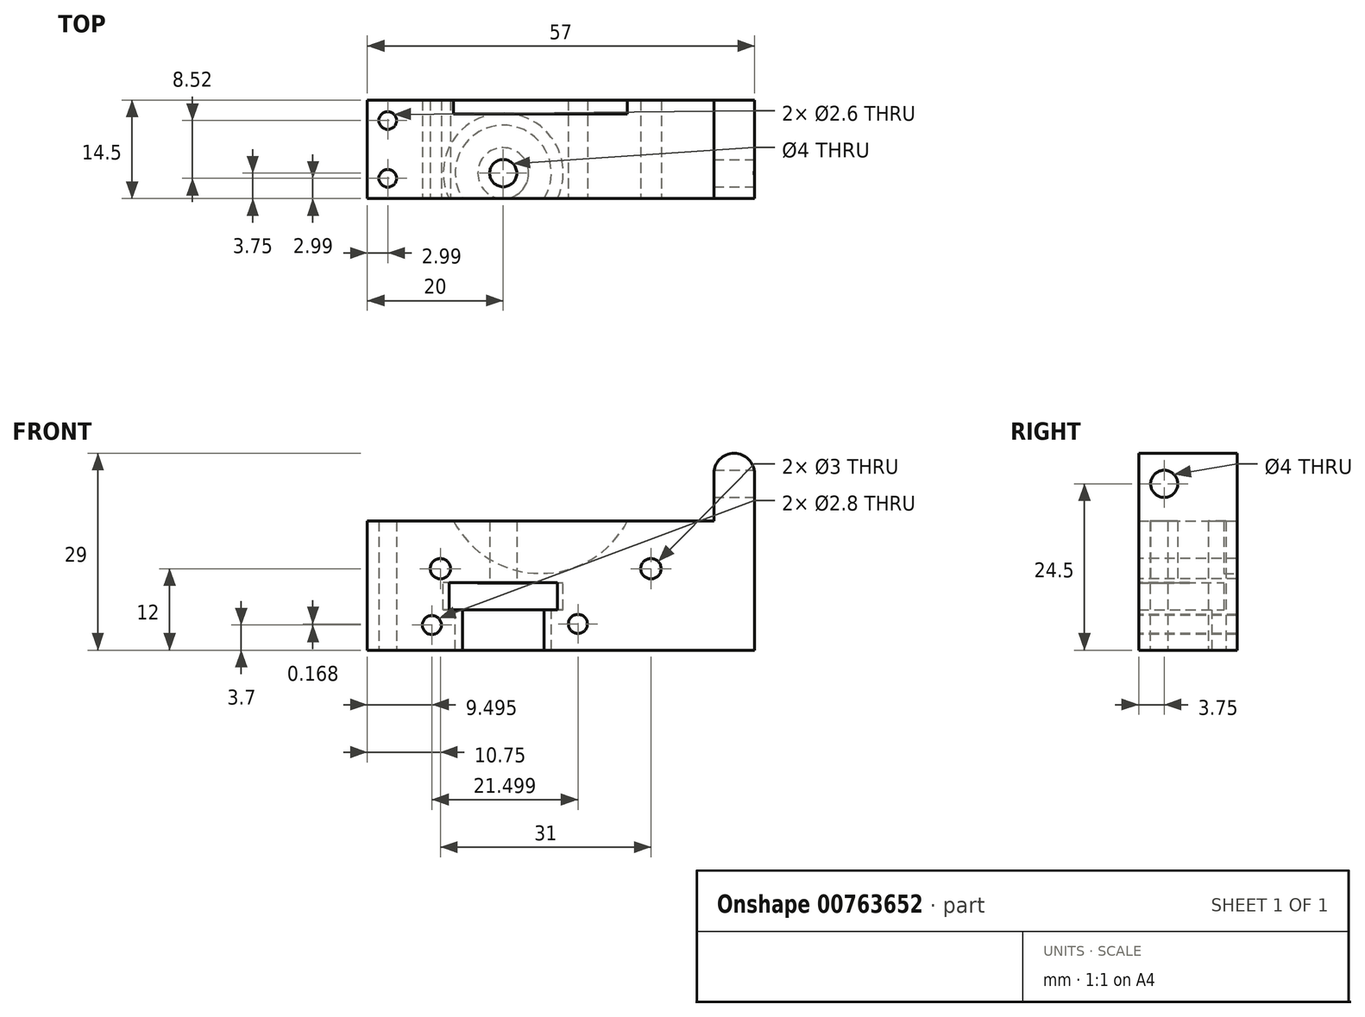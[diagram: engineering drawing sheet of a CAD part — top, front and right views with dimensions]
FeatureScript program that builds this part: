
annotation { "Feature Type Name" : "Feature", "Feature Type Description" : "" }
export const myFeature = defineFeature(function(context is Context, id is Id, definition is map)
    precondition{}
    {
        {
            var Q0;
            Q0=qCreatedBy(makeId("Top.planeOp"),FACE);
            var sketch = newSketch(context, id + "F0", { "sketchPlane" : qUnion([Q0])});
            skCircle(sketch, "E0", {"center": v(0, 0) * mm, "radius": 2 * mm});
            skLineSegment(sketch, "E1", {"start": v(27, -3.75) * mm, "end": v(-20, -3.75) * mm});
            skLineSegment(sketch, "E2", {"start": v(-20, -3.75) * mm, "end": v(-20, 10.75) * mm});
            skLineSegment(sketch, "E3", {"start": v(-20, 10.75) * mm, "end": v(27, 10.75) * mm});
            skLineSegment(sketch, "E4", {"start": v(27, 10.75) * mm, "end": v(27, -3.75) * mm});
            skCircle(sketch, "E5", {"center": v(-17.01, 7.76) * mm, "radius": 1.3 * mm});
            skCircle(sketch, "E6", {"center": v(-17.01, -0.76) * mm, "radius": 1.3 * mm});
            skSolve(sketch);
        }
        {
            var Q0;
            Q0=makeQuery(id+"F0.imprint","IMPRINT",FACE,{"disambiguationData":[TD([[makeQuery(id+"F0.imprint","IMPRINT",EDGE,{"derivedFrom":sQuery(id+"F0.wireOp",EDGE,"E0")}),-1.0]])]});
            extrude(context, id + "F1", {"entities" : qUnion([Q0]), "depth" : 19 * mm, "offsetDistance" : 25 * mm});
        }
        {
            var Q0;
            Q0=makeQuery(id+"F1.opExtrude","SWEPT_FACE",FACE,{"disambiguationData":[OSD([sQuery(id+"F0.wireOp",EDGE,"E1")])]});
            var sketch = newSketch(context, id + "F2", { "sketchPlane" : qUnion([Q0])});
            skLineSegment(sketch, "E7", {"start": v(0, 0) * mm, "end": v(0, 19) * mm, "construction": true});
            skLineSegment(sketch, "E8", {"start": v(-8, 9.93) * mm, "end": v(0, 9.93) * mm});
            skLineSegment(sketch, "E9", {"start": v(-8, 9.93) * mm, "end": v(-8, 5.98) * mm});
            skLineSegment(sketch, "E10", {"start": v(-8, 5.98) * mm, "end": v(-6, 5.98) * mm});
            skLineSegment(sketch, "E11", {"start": v(-6, 5.98) * mm, "end": v(-6, 0) * mm});
            skLineSegment(sketch, "E12", {"start": v(-6, 0) * mm, "end": v(0, 0) * mm});
            skLineSegment(sketch, "E13", {"start": v(0, 9.93) * mm, "end": v(0, 0) * mm});
            skPoint(sketch, "E14", {"position": v(16.46, 1136.01) * mm});
            skSolve(sketch);
        }
        {
            var Q0;
            Q0=makeQuery(id+"F2.imprint","IMPRINT",FACE,{"disambiguationData":[TD([[makeQuery(id+"F2.imprint","IMPRINT",EDGE,{"derivedFrom":sQuery(id+"F2.wireOp",EDGE,"E8")}),-1.0]])]});
            var Q1;
            Q1=makeQuery(id+"F1.opExtrude","CAP_EDGE",EDGE,{"disambiguationData":[OSD([sQuery(id+"F0.wireOp",EDGE,"E0")])],"isStart":true});
            revolve(context, id + "F3", {"operationType" : NewBodyOperationType.REMOVE, "surfaceOperationType" : NewSurfaceOperationType.NEW, "entities" : qUnion([Q0]), "axis" : qUnion([Q1]), "revolveType" : RevolveType.FULL, "oppositeDirection" : true});
        }
        {
            var Q0;
            {var subQ0=sQuery(id+"F0.wireOp",EDGE,"E0");Q0=makeQuery(id+"F3.boolean.opBoolean","SPLIT",FACE,{"disambiguationData":[TD([makeQuery(id+"F1.opExtrude","SWEPT_FACE",FACE,{"disambiguationData":[OSD([subQ0])]})])],"derivedFrom":makeQuery(id+"F1.opExtrude","CAP_FACE",FACE,{"disambiguationData":[OSD([subQ0,sQuery(id+"F0.wireOp",EDGE,"E1"),sQuery(id+"F0.wireOp",EDGE,"E2"),sQuery(id+"F0.wireOp",EDGE,"E3"),sQuery(id+"F0.wireOp",EDGE,"E4"),sQuery(id+"F0.wireOp",EDGE,"E5"),sQuery(id+"F0.wireOp",EDGE,"E6")])],"isStart":true})});}
            extrude(context, id + "F4", {"entities" : qUnion([Q0]), "operationType" : NewBodyOperationType.REMOVE, "oppositeDirection" : true, "depth" : 9.9 * mm, "offsetDistance" : 25 * mm});
        }
        {
            var Q0;
            Q0=makeQuery(id+"F1.opExtrude","SWEPT_FACE",FACE,{"disambiguationData":[OSD([sQuery(id+"F0.wireOp",EDGE,"E1")])]});
            var sketch = newSketch(context, id + "F5", { "sketchPlane" : qUnion([Q0])});
            skCircle(sketch, "E15", {"center": v(-10.5, 3.7) * mm, "radius": 1.4 * mm});
            skCircle(sketch, "E16.1.0.0", {"center": v(11, 3.87) * mm, "radius": 1.4 * mm});
            skLineSegment(sketch, "E16.direction1", {"start": v(-10.5, 3.7) * mm, "end": v(11, 3.87) * mm, "construction": true});
            skCircle(sketch, "E17", {"center": v(-9.25, 12) * mm, "radius": 1.5 * mm});
            skCircle(sketch, "E18", {"center": v(21.75, 12) * mm, "radius": 1.5 * mm});
            skSolve(sketch);
        }
        {
            var Q0;
            Q0=makeQuery(id+"F5.imprint","IMPRINT",FACE,{"disambiguationData":[TD([[makeQuery(id+"F5.imprint","IMPRINT",EDGE,{"derivedFrom":sQuery(id+"F5.wireOp",EDGE,"E17")}),1.0]])]});
            var Q1;
            Q1=makeQuery(id+"F5.imprint","IMPRINT",FACE,{"disambiguationData":[TD([[makeQuery(id+"F5.imprint","IMPRINT",EDGE,{"derivedFrom":sQuery(id+"F5.wireOp",EDGE,"E15")}),1.0]])]});
            var Q2;
            Q2=makeQuery(id+"F5.imprint","IMPRINT",FACE,{"disambiguationData":[TD([[makeQuery(id+"F5.imprint","IMPRINT",EDGE,{"derivedFrom":sQuery(id+"F5.wireOp",EDGE,"E16.1.0.0")}),1.0]])]});
            var Q3;
            Q3=makeQuery(id+"F5.imprint","IMPRINT",FACE,{"disambiguationData":[TD([[makeQuery(id+"F5.imprint","IMPRINT",EDGE,{"derivedFrom":sQuery(id+"F5.wireOp",EDGE,"E18")}),1.0]])]});
            var Q4;
            Q4=makeQuery(id+"F1.opExtrude","SWEPT_FACE",FACE,{"disambiguationData":[OSD([sQuery(id+"F0.wireOp",EDGE,"E3")])]});
            extrude(context, id + "F6", {"entities" : qUnion([Q0, Q1, Q2, Q3]), "operationType" : NewBodyOperationType.REMOVE, "endBound" : BoundingType.UP_TO_SURFACE, "oppositeDirection" : true, "depth" : 18.4 * mm, "endBoundEntityFace" : qUnion([Q4]), "offsetDistance" : 25 * mm});
        }
        {
            var Q0;
            Q0=makeQuery(id+"F1.opExtrude","SWEPT_FACE",FACE,{"disambiguationData":[OSD([sQuery(id+"F0.wireOp",EDGE,"E4")])]});
            extrude(context, id + "F7", {"entities" : qUnion([Q0]), "operationType" : NewBodyOperationType.ADD, "depth" : 10 * mm, "offsetDistance" : 25 * mm});
        }
        {
            var Q0;
            {var subQ0=sQuery(id+"F0.wireOp",EDGE,"E4");Q0=makeQuery(id+"F7.boolean.opBoolean","MERGE",FACE,{"derivedFrom":[makeQuery(id+"F1.opExtrude","CAP_FACE",FACE,{"disambiguationData":[OSD([sQuery(id+"F0.wireOp",EDGE,"E0"),sQuery(id+"F0.wireOp",EDGE,"E1"),sQuery(id+"F0.wireOp",EDGE,"E2"),sQuery(id+"F0.wireOp",EDGE,"E3"),subQ0,sQuery(id+"F0.wireOp",EDGE,"E5"),sQuery(id+"F0.wireOp",EDGE,"E6")])],"isStart":false}),makeQuery(id+"F7.opExtrude","SWEPT_FACE",FACE,{"disambiguationData":[OSD([subQ0]),TDD([makeQuery(id+"F1.opExtrude","CAP_EDGE",EDGE,{"disambiguationData":[OSD([subQ0])],"isStart":false})])]})]});}
            var sketch = newSketch(context, id + "F8", { "sketchPlane" : qUnion([Q0])});
            skLineSegment(sketch, "E19", {"start": v(31, 10.75) * mm, "end": v(31, -3.75) * mm});
            skSolve(sketch);
        }
        {
            var Q0;
            {var subQ0=sQuery(id+"F8.wireOp",EDGE,"E19");Q0=makeQuery(id+"F8.imprint","IMPRINT",FACE,{"disambiguationData":[TD([[makeQuery(id+"F8.imprint","IMPRINT",EDGE,{"derivedFrom":subQ0}),1.0]])]});}
            extrude(context, id + "F9", {"entities" : qUnion([Q0]), "operationType" : NewBodyOperationType.ADD, "depth" : (10) * mm, "offsetDistance" : 25 * mm});
        }
        {
            var Q0;
            {var subQ0=sQuery(id+"F0.wireOp",EDGE,"E4");Q0=makeQuery(id+"F9.boolean.opBoolean","MERGE",FACE,{"derivedFrom":[makeQuery(id+"F7.opExtrude","CAP_FACE",FACE,{"disambiguationData":[OSD([subQ0])],"isStart":false}),makeQuery(id+"F9.opExtrude","SWEPT_FACE",FACE,{"disambiguationData":[OSD([subQ0])]})]});}
            var sketch = newSketch(context, id + "F10", { "sketchPlane" : qUnion([Q0])});
            skCircle(sketch, "E20", {"center": v(0, 24.5) * mm, "radius": 2 * mm});
            skSolve(sketch);
        }
        {
            var Q0;
            Q0=makeQuery(id+"F10.imprint","IMPRINT",FACE,{"disambiguationData":[TD([[makeQuery(id+"F10.imprint","IMPRINT",EDGE,{"derivedFrom":sQuery(id+"F10.wireOp",EDGE,"E20")}),1.0]])]});
            var Q1;
            Q1=makeQuery(id+"F9.opExtrude","SWEPT_FACE",FACE,{"disambiguationData":[OSD([sQuery(id+"F8.wireOp",EDGE,"E19")])]});
            extrude(context, id + "F11", {"entities" : qUnion([Q0]), "operationType" : NewBodyOperationType.REMOVE, "endBound" : BoundingType.UP_TO_SURFACE, "oppositeDirection" : true, "depth" : 25 * mm, "endBoundEntityFace" : qUnion([Q1]), "offsetDistance" : 25 * mm});
        }
        {
            var Q0;
            Q0=makeQuery(id+"F9.opExtrude","CAP_EDGE",EDGE,{"disambiguationData":[OSD([sQuery(id+"F8.wireOp",EDGE,"E19")])],"isStart":false});
            var Q1;
            Q1=makeQuery(id+"F9.opExtrude","CAP_EDGE",EDGE,{"disambiguationData":[OSD([sQuery(id+"F0.wireOp",EDGE,"E4")])],"isStart":false});
            fillet(context, id + "F12", {"entities" : qUnion([Q0, Q1]), "radius" : (3) * mm, "tangentPropagation" : true, "allowEdgeOverflow" : false});
        }
        {
            var Q0;
            {var subQ0=sQuery(id+"F0.wireOp",EDGE,"E4");var subQ1=sQuery(id+"F0.wireOp",EDGE,"E3");Q0=makeQuery(id+"F9.boolean.opBoolean","MERGE",FACE,{"derivedFrom":[makeQuery(id+"F7.boolean.opBoolean","MERGE",FACE,{"derivedFrom":[makeQuery(id+"F1.opExtrude","SWEPT_FACE",FACE,{"disambiguationData":[OSD([subQ1])]}),makeQuery(id+"F7.opExtrude","SWEPT_FACE",FACE,{"disambiguationData":[OSD([subQ1,subQ0])]})]}),makeQuery(id+"F9.opExtrude","SWEPT_FACE",FACE,{"disambiguationData":[OSD([subQ1,subQ0])]})]});}
            var sketch = newSketch(context, id + "F13", { "sketchPlane" : qUnion([Q0])});
            skLineSegment(sketch, "E21", {"start": v(-5.5, 19) * mm, "end": v(-5.5, 7.75) * mm, "construction": true});
            skCircle(sketch, "E22", {"center": v(-5.5, 25.8) * mm, "radius": 14.48 * mm});
            skSolve(sketch);
        }
        {
            var Q0;
            {var subQ0=sQuery(id+"F13.wireOp",EDGE,"E22");var subQ1=sQuery(id+"F0.wireOp",EDGE,"E4");var subQ2=sQuery(id+"F0.wireOp",EDGE,"E3");var subQ3=makeQuery(id+"F7.boolean.opBoolean","MERGE",EDGE,{"derivedFrom":[makeQuery(id+"F1.opExtrude","CAP_EDGE",EDGE,{"disambiguationData":[OSD([subQ2])],"isStart":false}),makeQuery(id+"F7.opExtrude","SWEPT_EDGE",EDGE,{"disambiguationData":[OSD([subQ2,subQ1]),TDD([makeQuery(id+"F1.opExtrude","CAP_VERTEX",VERTEX,{"disambiguationData":[OSD([subQ2,subQ1])],"isStart":false})])]})]});var subQ4=makeQuery(id+"F13.imprint","INTERSECT",VERTEX,{"disambiguationData":[OD(0.0)],"derivedFrom":[subQ3,subQ0]});Q0=makeQuery(id+"F13.imprint","IMPRINT",FACE,{"disambiguationData":[TD([[makeQuery(id+"F13.imprint","IMPRINT",EDGE,{"disambiguationData":[TD([[subQ4,1.0]])],"derivedFrom":subQ0}),1.0]])]});}
            extrude(context, id + "F14", {"entities" : qUnion([Q0]), "operationType" : NewBodyOperationType.REMOVE, "oppositeDirection" : true, "depth" : (2) * mm, "offsetDistance" : 25 * mm});
        }
    });
